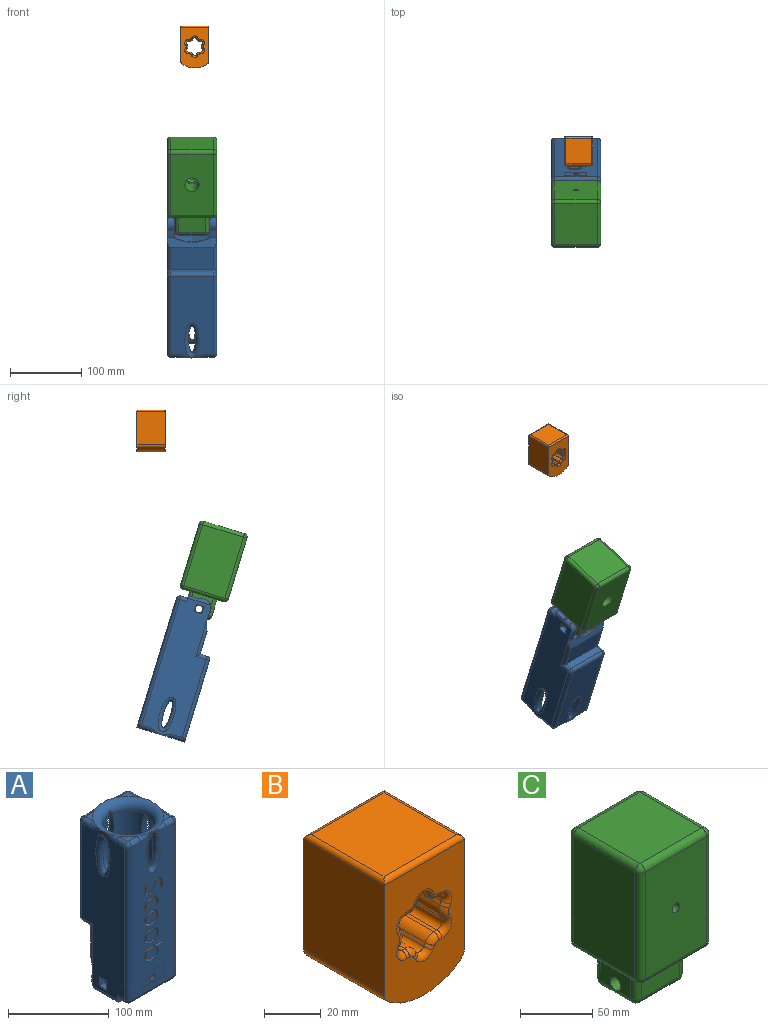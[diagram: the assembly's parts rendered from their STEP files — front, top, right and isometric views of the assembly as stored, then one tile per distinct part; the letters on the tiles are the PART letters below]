
ASSEMBLY  parts=3 mates=1
PART A: 199 faces, bbox 111.1x111.1x220.2 mm
  f0: plane 215x80mm, normal (-1,0,0), area 9348.8mm2, adj f3,f12,f14,f16,f42,f46,f49,f50
  f1: plane 60x32.41mm, normal (0,1,0), area 1944.7mm2, adj f10,f16,f28,f191
  f2: plane 10x8.52mm, normal (0,-1,0), area 37.4mm2, adj f4,f7,f30,f59,f197
  f3: plane 10x8.52mm, normal (0,-1,0), area 37.4mm2, adj f0,f12,f30,f56,f195
  f4: plane 215x80mm, normal (1,0,0), area 9383.2mm2, adj f2,f7,f8,f10,f24,f34,f36,f39
  f5: plane 60x45mm, normal (-1,0,0), area 792.6mm2, adj f7,f9,f11,f24,f29,f30,f31,f68
  f6: plane 60x45mm, normal (1,0,0), area 792.6mm2, adj f12,f15,f17,f23,f29,f30,f31,f68
  f7: cylinder r=5mm len=33.8mm, axis (0,-1,0), area 340.7mm2, adj f2,f4,f5,f194,f197,f198
  f8: cylinder r=5mm len=11.1mm, axis (0,0,-1), area 0mm2, adj f4,f194
  f9: cylinder r=5mm len=11.1mm, axis (0,0,-1), area 0mm2, adj f5,f194
  f10: cylinder r=5mm len=50.66mm, axis (0,0,-1), area 326.2mm2, adj f1,f4,f39,f191
  f11: cylinder r=5mm len=0.66mm, axis (0,0,-1), area 0.1mm2, adj f5,f13,f191
  f12: cylinder r=5mm len=33.8mm, axis (0,-1,0), area 340.7mm2, adj f0,f3,f6,f192,f195,f196
  f13: bspline ~64.63x12.82mm, area 80.3mm2, adj f11,f17,f31,f191
  f14: cylinder r=5mm len=11.1mm, axis (0,0,1), area 0mm2, adj f0,f192
  f15: cylinder r=5mm len=11.1mm, axis (0,0,1), area 0mm2, adj f6,f192
  f16: cylinder r=5mm len=50.66mm, axis (0,0,1), area 326.2mm2, adj f0,f1,f42,f191
  f17: cylinder r=5mm len=0.66mm, axis (0,0,1), area 0.1mm2, adj f6,f13,f191
  f18: plane 190x60mm, normal (0,-1,0), area 8811.1mm2, adj f52,f54,f57,f60,f64,f66,f67,f76
  f19: plane 11.97x11.97mm, normal (0,0,1), area 59.9mm2, adj f32,f63,f66
  f20: plane 11.97x11.97mm, normal (0,0,1), area 59.9mm2, adj f32,f53,f54
  f21: plane 11.97x11.97mm, normal (0,0,1), area 59.9mm2, adj f32,f47,f49
  f22: plane 120x60mm, normal (0,1,0), area 6147.2mm2, adj f35,f37,f40,f43,f45,f46,f47,f73
  f23: cylinder r=5.25mm len=10.5mm, axis (-1,0,0), area 99mm2, adj f6,f189
  f24: cylinder r=5.25mm len=10.5mm, axis (-1,0,0), area 329.9mm2, adj f4,f5
  f25: plane 11.97x11.97mm, normal (0,0,1), area 59.9mm2, adj f32,f36,f37
  f26: cylinder r=25mm len=105mm, axis (0,0,1), area 15263.1mm2, adj f32,f33,f69,f70,f71,f72
  f27: plane 40x40mm, normal (0,0,1), area 1256.6mm2, adj f33
  f28: plane 60x10mm, normal (0,0,-1), area 600mm2, adj f1,f39,f42,f43
  f29: plane 50x25.26mm, normal (0,1,0), area 979.4mm2, adj f5,f6,f31,f68,f184
  f30: plane 60x10mm, normal (0,0,-1), area 350mm2, adj f2,f3,f5,f6,f56,f59,f60,f68
  f31: extruded ~50x35mm, area 1791.2mm2, adj f5,f6,f13,f29
  f32: torus R=35mm, axis (0,0,-1), area 2792.6mm2, adj f19,f20,f21,f25,f26,f34,f35,f45
  f33: torus R=20mm, axis (0,0,1), area 1144mm2, adj f26,f27
  f34: bspline ~18.62x5.29mm, area 43.9mm2, adj f4,f32,f36
  f35: bspline ~18.62x5.29mm, area 45.1mm2, adj f22,f32,f37
  f36: cylinder r=5mm len=11.97mm, axis (0,-1,0), area 94mm2, adj f4,f25,f34,f38
  f37: cylinder r=5mm len=11.97mm, axis (1,0,0), area 94mm2, adj f22,f25,f35,f38
  f38: sphere r=5mm, area 39.3mm2, adj f36,f37,f40
  f39: cylinder r=5mm len=15mm, axis (0,-1,0), area 98.2mm2, adj f4,f10,f28,f41
  f40: cylinder r=5mm len=115mm, axis (0,0,-1), area 903.2mm2, adj f4,f22,f38,f41
  f41: sphere r=5mm, area 39.3mm2, adj f39,f40,f43
  f42: cylinder r=5mm len=15mm, axis (0,1,0), area 98.2mm2, adj f0,f16,f28,f44
  f43: cylinder r=5mm len=60mm, axis (-1,0,0), area 471.2mm2, adj f22,f28,f41,f44
  f44: sphere r=5mm, area 49.3mm2, adj f42,f43,f46
  f45: bspline ~18.03x5mm, area 45.1mm2, adj f22,f32,f47
  f46: cylinder r=5mm len=115mm, axis (0,0,1), area 903.2mm2, adj f0,f22,f44,f48
  f47: cylinder r=5mm len=11.97mm, axis (1,0,0), area 94mm2, adj f21,f22,f45,f48
  f48: sphere r=5mm, area 39.3mm2, adj f46,f47,f49
  f49: cylinder r=5mm len=11.97mm, axis (0,1,0), area 94mm2, adj f0,f21,f48,f50
  f50: bspline ~18.03x5mm, area 43.9mm2, adj f0,f32,f49
  f51: bspline ~18.03x5mm, area 45.1mm2, adj f0,f32,f53
  f52: bspline ~18.62x5.29mm, area 45.1mm2, adj f18,f32,f54
  f53: cylinder r=5mm len=11.97mm, axis (0,1,0), area 94mm2, adj f0,f20,f51,f55
  f54: cylinder r=5mm len=11.97mm, axis (-1,0,0), area 94mm2, adj f18,f20,f52,f55
  f55: sphere r=5mm, area 53.5mm2, adj f53,f54,f57
  f56: cylinder r=5mm len=10mm, axis (0,1,0), area 78.5mm2, adj f0,f3,f30,f58
  f57: cylinder r=5mm len=185mm, axis (0,0,-1), area 1453mm2, adj f0,f18,f55,f58
  f58: sphere r=5mm, area 53.5mm2, adj f56,f57,f60
  f59: cylinder r=5mm len=10mm, axis (0,-1,0), area 78.5mm2, adj f2,f4,f30,f62
  f60: cylinder r=5mm len=60mm, axis (-1,0,0), area 471.2mm2, adj f18,f30,f58,f62
  f61: bspline ~18.62x5.29mm, area 45.1mm2, adj f4,f32,f63
  f62: sphere r=5mm, area 25mm2, adj f59,f60,f64
  f63: cylinder r=5mm len=11.97mm, axis (0,-1,0), area 94mm2, adj f4,f19,f61,f65
  f64: cylinder r=5mm len=185mm, axis (0,0,1), area 1453mm2, adj f4,f18,f62,f65
  f65: sphere r=5mm, area 25mm2, adj f63,f64,f66
  f66: cylinder r=5mm len=11.97mm, axis (-1,0,0), area 94mm2, adj f18,f19,f65,f67
  f67: bspline ~18.03x5mm, area 45.1mm2, adj f18,f32,f66
  f68: cylinder r=5mm len=50mm, axis (-1,0,0), area 392.7mm2, adj f5,f6,f29,f30
  f69: extruded ~39.82x9.96mm, area 457.4mm2, adj f26,f32,f73
  f70: extruded ~39.82x9.96mm, area 457.4mm2, adj f26,f32,f76
  f71: extruded ~39.82x9.96mm, area 456.4mm2, adj f26,f75
  f72: extruded ~40x10mm, area 456.5mm2, adj f26,f74
  f73: bspline ~50x20.01mm, area 763.5mm2, adj f22,f69
  f74: bspline ~50x20.01mm, area 763.5mm2, adj f0,f72
  f75: bspline ~50x20.01mm, area 763.5mm2, adj f4,f71
  f76: bspline ~50x20.01mm, area 763.5mm2, adj f18,f70
  f77: plane 30x15mm, normal (0,-1,0), area 405.8mm2, adj f18,f183
  f78: extruded ~7.08x5.13mm, area 39.1mm2, adj f18,f79,f94,f95
  f79: extruded ~6.25x5.13mm, area 35.9mm2, adj f18,f78,f80,f95
  f80: extruded ~6.36x5.13mm, area 36.3mm2, adj f18,f79,f81,f95
  f81: extruded ~7.14x5.13mm, area 39.4mm2, adj f18,f80,f82,f95
  f82: extruded ~5.17x5.13mm, area 27.3mm2, adj f18,f81,f83,f95
  f83: extruded ~5.13x3.39mm, area 23.6mm2, adj f18,f82,f84,f95
  f84: extruded ~5.13x4.47mm, area 24mm2, adj f18,f83,f85,f95
  f85: extruded ~6.38x5.13mm, area 36.4mm2, adj f18,f84,f94,f95
  f86: extruded ~5.45x5.13mm, area 29.4mm2, adj f87,f93,f95,f180
  f87: extruded ~5.13x4.21mm, area 24.4mm2, adj f86,f88,f95,f180
  f88: extruded ~5.13x4.27mm, area 24.8mm2, adj f87,f89,f95,f180
  f89: extruded ~5.43x5.13mm, area 29.4mm2, adj f88,f90,f95,f180
  f90: extruded ~5.48x5.13mm, area 29.6mm2, adj f89,f91,f95,f180
  f91: extruded ~5.13x4.24mm, area 24.7mm2, adj f90,f92,f95,f180
  f92: extruded ~5.13x4.22mm, area 24.6mm2, adj f91,f93,f95,f180
  f93: extruded ~5.48x5.13mm, area 29.6mm2, adj f86,f92,f95,f180
  f94: extruded ~7.16x5.13mm, area 39.5mm2, adj f18,f78,f85,f95
  f95: plane 19.43x17.22mm, normal (0,-1,0), area 134.9mm2, adj f78,f79,f80,f81,f82,f83,f84,f85
  f96: extruded ~7.08x5.13mm, area 39.1mm2, adj f18,f97,f112,f113
  f97: extruded ~6.25x5.13mm, area 35.9mm2, adj f18,f96,f98,f113
  f98: extruded ~6.36x5.13mm, area 36.3mm2, adj f18,f97,f99,f113
  f99: extruded ~7.14x5.13mm, area 39.4mm2, adj f18,f98,f100,f113
  f100: extruded ~5.17x5.13mm, area 27.3mm2, adj f18,f99,f101,f113
  f101: extruded ~5.13x3.39mm, area 23.6mm2, adj f18,f100,f102,f113
  f102: extruded ~5.13x4.47mm, area 24mm2, adj f18,f101,f103,f113
  f103: extruded ~6.38x5.13mm, area 36.4mm2, adj f18,f102,f112,f113
  f104: extruded ~5.45x5.13mm, area 29.4mm2, adj f105,f111,f113,f181
  f105: extruded ~5.13x4.21mm, area 24.4mm2, adj f104,f106,f113,f181
  f106: extruded ~5.13x4.27mm, area 24.8mm2, adj f105,f107,f113,f181
  f107: extruded ~5.43x5.13mm, area 29.4mm2, adj f106,f108,f113,f181
  f108: extruded ~5.48x5.13mm, area 29.6mm2, adj f107,f109,f113,f181
  f109: extruded ~5.13x4.24mm, area 24.7mm2, adj f108,f110,f113,f181
  f110: extruded ~5.13x4.22mm, area 24.6mm2, adj f109,f111,f113,f181
  f111: extruded ~5.48x5.13mm, area 29.6mm2, adj f104,f110,f113,f181
  f112: extruded ~7.16x5.13mm, area 39.5mm2, adj f18,f96,f103,f113
  f113: plane 19.43x17.22mm, normal (0,-1,0), area 134.9mm2, adj f96,f97,f98,f99,f100,f101,f102,f103
  f114: extruded ~5.13x4.73mm, area 25.1mm2, adj f18,f115,f128,f129
  f115: plane 5.13x2.51mm, normal (0,0,1), area 12.9mm2, adj f18,f114,f116,f129
  f116: extruded ~5.13x4.81mm, area 25.4mm2, adj f18,f115,f117,f129
  f117: extruded ~5.13x4.13mm, area 24.1mm2, adj f18,f116,f118,f129
  f118: extruded ~5.3x5.13mm, area 28.6mm2, adj f18,f117,f119,f129
  f119: extruded ~7.28x5.71mm, area 54.3mm2, adj f18,f118,f120,f129
  f120: extruded ~5.13x1.96mm, area 10.2mm2, adj f18,f119,f121,f129
  f121: extruded ~5.13x2.05mm, area 11mm2, adj f18,f120,f122,f129
  f122: plane 5.13x2.41mm, normal (0.34,0,0.94), area 13.1mm2, adj f18,f121,f123,f129
  f123: extruded ~5.13x2.12mm, area 11.5mm2, adj f18,f122,f124,f129
  f124: extruded ~5.13x2.7mm, area 14mm2, adj f18,f123,f125,f129
  f125: extruded ~6.46x5.13mm, area 36.8mm2, adj f18,f124,f126,f129
  f126: extruded ~7.27x5.13mm, area 40mm2, adj f18,f125,f127,f129
  f127: extruded ~7.09x5.13mm, area 39mm2, adj f18,f126,f128,f129
  f128: extruded ~6.3x5.13mm, area 35.9mm2, adj f18,f114,f127,f129
  f129: plane 19.43x13.54mm, normal (0,-1,0), area 93.2mm2, adj f114,f115,f116,f117,f118,f119,f120,f121
  f130: extruded ~5.88x5.13mm, area 34.9mm2, adj f18,f131,f152,f153
  f131: plane 5.13x0.14mm, normal (-1,0,0), area 0.7mm2, adj f18,f130,f132,f153
  f132: extruded ~5.13x3.9mm, area 20mm2, adj f18,f131,f133,f153
  f133: plane 6.47x5.13mm, normal (0,0,1), area 33.2mm2, adj f18,f132,f134,f153
  f134: plane 5.13x2.84mm, normal (-1,0,0), area 14.6mm2, adj f18,f133,f135,f153
  f135: plane 26.61x5.13mm, normal (0,0,-1), area 136.6mm2, adj f18,f134,f136,f153
  f136: plane 5.13x2.04mm, normal (1,0,0), area 10.5mm2, adj f18,f135,f137,f153
  f137: plane 5.13x2.41mm, normal (0.24,0,0.97), area 12.8mm2, adj f18,f136,f138,f153
  f138: plane 5.13x0.21mm, normal (1,0,0), area 1.1mm2, adj f18,f137,f139,f153
  f139: extruded ~5.13x2.54mm, area 17mm2, adj f18,f138,f140,f153
  f140: extruded ~5.13x3.35mm, area 17.7mm2, adj f18,f139,f141,f153
  f141: extruded ~5.72x5.13mm, area 33.4mm2, adj f18,f140,f142,f153
  f142: extruded ~7.18x5.13mm, area 39.1mm2, adj f18,f141,f143,f153
  f143: extruded ~7.14x5.13mm, area 38.9mm2, adj f18,f142,f152,f153
  f144: extruded ~5.13x3.97mm, area 23.3mm2, adj f145,f151,f153,f182
  f145: extruded ~5.46x5.13mm, area 29.2mm2, adj f144,f146,f153,f182
  f146: extruded ~5.48x5.13mm, area 29.3mm2, adj f145,f147,f153,f182
  f147: extruded ~5.13x3.9mm, area 23.3mm2, adj f146,f148,f153,f182
  f148: extruded ~5.13x4.22mm, area 24.2mm2, adj f147,f149,f153,f182
  f149: extruded ~5.65x5.13mm, area 30.3mm2, adj f148,f150,f153,f182
  f150: extruded ~5.62x5.13mm, area 30.1mm2, adj f149,f151,f153,f182
  f151: extruded ~5.13x4.19mm, area 24mm2, adj f144,f150,f153,f182
  f152: extruded ~5.74x5.13mm, area 33.3mm2, adj f18,f130,f143,f153
  f153: plane 26.96x16.51mm, normal (0,-1,0), area 170.7mm2, adj f130,f131,f132,f133,f134,f135,f136,f137
  f154: extruded ~5.13x4.17mm, area 23.3mm2, adj f18,f155,f178,f179
  f155: extruded ~5.41x5.13mm, area 32.1mm2, adj f18,f154,f156,f179
  f156: extruded ~5.13x3.48mm, area 19.5mm2, adj f18,f155,f157,f179
  f157: extruded ~5.13x1.62mm, area 11.5mm2, adj f18,f156,f158,f179
  f158: extruded ~5.13x2.13mm, area 11.3mm2, adj f18,f157,f159,f179
  f159: extruded ~5.13x2.75mm, area 16.2mm2, adj f18,f158,f160,f179
  f160: extruded ~5.13x3.61mm, area 19.6mm2, adj f18,f159,f161,f179
  f161: extruded ~6.02x5.13mm, area 31.8mm2, adj f18,f160,f162,f179
  f162: plane 5.13x2.53mm, normal (0.34,0,0.94), area 13.8mm2, adj f18,f161,f163,f179
  f163: extruded ~6.86x5.13mm, area 36.2mm2, adj f18,f162,f164,f179
  f164: extruded ~5.75x5.13mm, area 31.4mm2, adj f18,f163,f165,f179
  f165: extruded ~5.13x4.6mm, area 27.1mm2, adj f18,f164,f166,f179
  f166: extruded ~5.13x4.46mm, area 24.7mm2, adj f18,f165,f167,f179
  f167: extruded ~5.13x4.98mm, area 30mm2, adj f18,f166,f168,f179
  f168: extruded ~5.13x3.72mm, area 20.8mm2, adj f18,f167,f169,f179
  f169: extruded ~5.13x1.75mm, area 12mm2, adj f18,f168,f170,f179
  f170: extruded ~5.13x2.13mm, area 11.4mm2, adj f18,f169,f171,f179
  f171: extruded ~5.13x3.07mm, area 18.2mm2, adj f18,f170,f172,f179
  f172: extruded ~5.13x4.38mm, area 23.6mm2, adj f18,f171,f173,f179
  f173: extruded ~5.13x3.59mm, area 18.6mm2, adj f18,f172,f174,f179
  f174: extruded ~5.13x3.35mm, area 18mm2, adj f18,f173,f175,f179
  f175: plane 5.13x2.8mm, normal (0,0,-1), area 14.4mm2, adj f18,f174,f176,f179
  f176: extruded ~6.84x5.13mm, area 35.9mm2, adj f18,f175,f177,f179
  f177: extruded ~6.5x5.13mm, area 35.3mm2, adj f18,f176,f178,f179
  f178: extruded ~5.15x5.13mm, area 30.3mm2, adj f18,f154,f177,f179
  f179: plane 25.7x15.73mm, normal (0,-1,0), area 144.7mm2, adj f154,f155,f156,f157,f158,f159,f160,f161
  f180: plane 14.64x11.34mm, normal (0,-1,0), area 137.7mm2, adj f86,f87,f88,f89,f90,f91,f92,f93
  f181: plane 14.64x11.34mm, normal (0,-1,0), area 137.7mm2, adj f104,f105,f106,f107,f108,f109,f110,f111
  f182: plane 14.64x10.72mm, normal (0,-1,0), area 132.2mm2, adj f144,f145,f146,f147,f148,f149,f150,f151
  f183: cylinder r=3.75mm len=11.25mm, axis (0,1,0), area 265.1mm2, adj f77,f184
  f184: cone r=3.75mm half-angle=45deg, axis (0,1,0), area 187.4mm2, adj f29,f183
  f185: plane 11x7mm, normal (0,0,-1), area 77mm2, adj f0,f186,f188,f189
  f186: plane 11x7mm, normal (0,-1,0), area 77mm2, adj f0,f185,f187,f189
  f187: plane 11x7mm, normal (0,0,1), area 77mm2, adj f0,f186,f188,f189
  f188: plane 11x7mm, normal (0,1,0), area 77mm2, adj f0,f185,f187,f189
  f189: plane 11x11mm, normal (-1,0,0), area 34.4mm2, adj f23,f185,f186,f187,f188
  f190: plane 11.12x10mm, normal (0,1,0), area 111.2mm2, adj f0,f6,f191,f192
  f191: plane 75.57x18.81mm, normal (0,0.94,-0.35), area 742.8mm2, adj f1,f10,f11,f13,f16,f17,f190,f193
  f192: cylinder r=13.47mm len=18.23mm, axis (1,0,0), area 199.7mm2, adj f0,f6,f12,f14,f15,f190
  f193: plane 11.12x10mm, normal (0,1,0), area 111.2mm2, adj f4,f5,f191,f194
  f194: cylinder r=13.47mm len=18.23mm, axis (1,0,0), area 199.7mm2, adj f4,f5,f7,f8,f9,f193
  f195: plane 15.23x7.1mm, normal (0,0,-1), area 108.2mm2, adj f3,f12,f196
  f196: cylinder r=13.47mm len=7.1mm, axis (1,0,0), area 15.3mm2, adj f12,f195
  f197: plane 15.23x7.1mm, normal (0,0,-1), area 108.2mm2, adj f2,f7,f198
  f198: cylinder r=13.47mm len=7.1mm, axis (1,0,0), area 15.3mm2, adj f7,f197
PART B: 84 faces, bbox 40x40x59.1 mm
  f0: plane 57.1x40mm, normal (0,-1,0), area 1580.3mm2, adj f2,f3,f5,f24,f25,f26,f27,f29
  f1: plane 57.1x40mm, normal (0,1,0), area 1580.3mm2, adj f2,f3,f5,f28,f32,f33,f37,f38
  f2: plane 47.1x40mm, normal (-1,0,0), area 1884mm2, adj f0,f1,f78,f81
  f3: plane 47.1x40mm, normal (1,0,0), area 1884mm2, adj f0,f1,f79,f82
  f4: plane 36x36mm, normal (0,0,1), area 1296mm2, adj f80,f81,f82,f83
  f5: cylinder r=30mm len=40mm, axis (0,-1,0), area 1544.4mm2, adj f0,f1,f78,f79
  f6: plane 35x1.35mm, normal (0.87,0,0.5), area 54.6mm2, adj f23,f52,f53,f62
  f7: plane 35x1.35mm, normal (-0.87,0,0.5), area 54.6mm2, adj f18,f43,f51,f52
  f8: plane 35x1.56mm, normal (0,0,1), area 54.6mm2, adj f18,f34,f35,f42
  f9: plane 35x1.35mm, normal (-0.87,0,-0.5), area 54.6mm2, adj f19,f26,f33,f34
  f10: plane 35x1.35mm, normal (-0.87,0,0.5), area 54.6mm2, adj f19,f25,f31,f32
  f11: plane 35x1.56mm, normal (0,0,-1), area 54.6mm2, adj f20,f30,f31,f41
  f12: plane 35x1.35mm, normal (-0.87,0,-0.5), area 54.6mm2, adj f20,f40,f49,f50
  f13: plane 35x1.35mm, normal (0.87,0,-0.5), area 54.6mm2, adj f21,f48,f49,f61
  f14: plane 35x1.56mm, normal (0,0,-1), area 54.6mm2, adj f21,f60,f69,f70
  f15: plane 35x1.35mm, normal (0.87,0,0.5), area 54.6mm2, adj f22,f59,f69,f75
  f16: plane 35x1.35mm, normal (0.87,0,-0.5), area 54.6mm2, adj f22,f64,f72,f76
  f17: plane 35x1.56mm, normal (0,0,1), area 54.6mm2, adj f23,f63,f71,f72
  f18: cylinder r=5mm len=35mm, axis (0,-1,0), area 183.3mm2, adj f7,f8,f39,f46
  f19: cylinder r=5mm len=35mm, axis (0,-1,0), area 183.3mm2, adj f9,f10,f24,f28
  f20: cylinder r=5mm len=35mm, axis (0,-1,0), area 183.3mm2, adj f11,f12,f36,f45
  f21: cylinder r=5mm len=35mm, axis (0,-1,0), area 183.3mm2, adj f13,f14,f54,f66
  f22: cylinder r=5mm len=35mm, axis (0,-1,0), area 183.3mm2, adj f15,f16,f58,f77
  f23: cylinder r=5mm len=35mm, axis (0,-1,0), area 183.3mm2, adj f6,f17,f57,f67
  f24: torus R=2.5mm, axis (0,1,0), area 16.8mm2, adj f0,f19,f25,f26
  f25: cylinder r=2.5mm len=2.94mm, axis (0.5,0,0.87), area 6.1mm2, adj f0,f10,f24,f27
  f26: cylinder r=2.5mm len=2.94mm, axis (-0.5,0,0.87), area 6.1mm2, adj f0,f9,f24,f29
  f27: torus R=5mm, axis (0,1,0), area 28mm2, adj f0,f25,f30,f31
  f28: torus R=2.5mm, axis (0,1,0), area 16.8mm2, adj f1,f19,f32,f33
  f29: torus R=5mm, axis (0,1,0), area 28mm2, adj f0,f26,f34,f35
  f30: cylinder r=2.5mm len=2.5mm, axis (-1,0,0), area 6.1mm2, adj f0,f11,f27,f36
  f31: cylinder r=2.5mm len=35mm, axis (0,-1,0), area 183.3mm2, adj f10,f11,f27,f37
  f32: cylinder r=2.5mm len=2.94mm, axis (0.5,0,0.87), area 6.1mm2, adj f1,f10,f28,f37
  f33: cylinder r=2.5mm len=2.94mm, axis (-0.5,0,0.87), area 6.1mm2, adj f1,f9,f28,f38
  f34: cylinder r=2.5mm len=35mm, axis (0,1,0), area 183.3mm2, adj f8,f9,f29,f38
  f35: cylinder r=2.5mm len=2.5mm, axis (1,0,0), area 6.1mm2, adj f0,f8,f29,f39
  f36: torus R=2.5mm, axis (0,1,0), area 16.8mm2, adj f0,f20,f30,f40
  f37: torus R=5mm, axis (0,1,0), area 28mm2, adj f1,f31,f32,f41
  f38: torus R=5mm, axis (0,1,0), area 28mm2, adj f1,f33,f34,f42
  f39: torus R=2.5mm, axis (0,1,0), area 16.8mm2, adj f0,f18,f35,f43
  f40: cylinder r=2.5mm len=2.94mm, axis (-0.5,0,0.87), area 6.1mm2, adj f0,f12,f36,f44
  f41: cylinder r=2.5mm len=2.5mm, axis (-1,0,0), area 6.1mm2, adj f1,f11,f37,f45
  f42: cylinder r=2.5mm len=2.5mm, axis (1,0,0), area 6.1mm2, adj f1,f8,f38,f46
  f43: cylinder r=2.5mm len=2.94mm, axis (0.5,0,0.87), area 6.1mm2, adj f0,f7,f39,f47
  f44: torus R=5mm, axis (0,1,0), area 28mm2, adj f0,f40,f48,f49
  f45: torus R=2.5mm, axis (0,1,0), area 16.8mm2, adj f1,f20,f41,f50
  f46: torus R=2.5mm, axis (0,1,0), area 16.8mm2, adj f1,f18,f42,f51
  f47: torus R=5mm, axis (0,1,0), area 28mm2, adj f0,f43,f52,f53
  f48: cylinder r=2.5mm len=2.94mm, axis (-0.5,0,-0.87), area 6.1mm2, adj f0,f13,f44,f54
  f49: cylinder r=2.5mm len=35mm, axis (0,-1,0), area 183.3mm2, adj f12,f13,f44,f55
  f50: cylinder r=2.5mm len=2.94mm, axis (-0.5,0,0.87), area 6.1mm2, adj f1,f12,f45,f55
  f51: cylinder r=2.5mm len=2.94mm, axis (0.5,0,0.87), area 6.1mm2, adj f1,f7,f46,f56
  f52: cylinder r=2.5mm len=35mm, axis (0,-1,0), area 183.3mm2, adj f6,f7,f47,f56
  f53: cylinder r=2.5mm len=2.94mm, axis (0.5,0,-0.87), area 6.1mm2, adj f0,f6,f47,f57
  f54: torus R=2.5mm, axis (0,1,0), area 16.8mm2, adj f0,f21,f48,f60
  f55: torus R=5mm, axis (0,1,0), area 28mm2, adj f1,f49,f50,f61
  f56: torus R=5mm, axis (0,1,0), area 28mm2, adj f1,f51,f52,f62
  f57: torus R=2.5mm, axis (0,1,0), area 16.8mm2, adj f0,f23,f53,f63
  f58: torus R=2.5mm, axis (0,1,0), area 16.8mm2, adj f0,f22,f59,f64
  f59: cylinder r=2.5mm len=2.94mm, axis (0.5,0,-0.87), area 6.1mm2, adj f0,f15,f58,f65
  f60: cylinder r=2.5mm len=2.5mm, axis (-1,0,0), area 6.1mm2, adj f0,f14,f54,f65
  f61: cylinder r=2.5mm len=2.94mm, axis (-0.5,0,-0.87), area 6.1mm2, adj f1,f13,f55,f66
  f62: cylinder r=2.5mm len=2.94mm, axis (0.5,0,-0.87), area 6.1mm2, adj f1,f6,f56,f67
  f63: cylinder r=2.5mm len=2.5mm, axis (1,0,0), area 6.1mm2, adj f0,f17,f57,f68
  f64: cylinder r=2.5mm len=2.94mm, axis (-0.5,0,-0.87), area 6.1mm2, adj f0,f16,f58,f68
  f65: torus R=5mm, axis (0,1,0), area 28mm2, adj f0,f59,f60,f69
  f66: torus R=2.5mm, axis (0,1,0), area 16.8mm2, adj f1,f21,f61,f70
  f67: torus R=2.5mm, axis (0,1,0), area 16.8mm2, adj f1,f23,f62,f71
  f68: torus R=5mm, axis (0,1,0), area 28mm2, adj f0,f63,f64,f72
  f69: cylinder r=2.5mm len=35mm, axis (0,1,0), area 183.3mm2, adj f14,f15,f65,f73
  f70: cylinder r=2.5mm len=2.5mm, axis (-1,0,0), area 6.1mm2, adj f1,f14,f66,f73
  f71: cylinder r=2.5mm len=2.5mm, axis (1,0,0), area 6.1mm2, adj f1,f17,f67,f74
  f72: cylinder r=2.5mm len=35mm, axis (0,-1,0), area 183.3mm2, adj f16,f17,f68,f74
  f73: torus R=5mm, axis (0,1,0), area 28mm2, adj f1,f69,f70,f75
  f74: torus R=5mm, axis (0,1,0), area 28mm2, adj f1,f71,f72,f76
  f75: cylinder r=2.5mm len=2.94mm, axis (0.5,0,-0.87), area 6.1mm2, adj f1,f15,f73,f77
  f76: cylinder r=2.5mm len=2.94mm, axis (-0.5,0,-0.87), area 6.1mm2, adj f1,f16,f74,f77
  f77: torus R=2.5mm, axis (0,1,0), area 16.8mm2, adj f1,f22,f75,f76
  f78: cylinder r=5mm len=40mm, axis (0,-1,0), area 185.5mm2, adj f0,f1,f2,f5
  f79: cylinder r=5mm len=40mm, axis (0,-1,0), area 185.5mm2, adj f0,f1,f3,f5
  f80: cylinder r=2mm len=40mm, axis (1,0,0), area 121.1mm2, adj f1,f4,f81,f82
  f81: cylinder r=2mm len=40mm, axis (0,1,0), area 121.1mm2, adj f2,f4,f80,f83
  f82: cylinder r=2mm len=40mm, axis (0,-1,0), area 121.1mm2, adj f3,f4,f80,f83
  f83: cylinder r=2mm len=40mm, axis (-1,0,0), area 121.1mm2, adj f0,f4,f81,f82
PART C: 48 faces, bbox 70x70x130 mm
  f0: plane 90x60mm, normal (0,-1,0), area 5355.8mm2, adj f32,f37,f40,f43,f46
  f1: plane 90x60mm, normal (-1,0,0), area 5400mm2, adj f29,f38,f39,f43
  f2: plane 90x60mm, normal (0,1,0), area 5085.8mm2, adj f24,f28,f29,f30,f44
  f3: plane 90x60mm, normal (1,0,0), area 5400mm2, adj f24,f27,f31,f32
  f4: plane 60x60mm, normal (0,0,-1), area 1701.5mm2, adj f6,f7,f8,f9,f12,f14,f17,f23
  f5: plane 60x60mm, normal (0,0,1), area 3600mm2, adj f30,f31,f39,f40
  f6: plane 30x25mm, normal (-1,0,0), area 663.9mm2, adj f4,f11,f14,f20,f23
  f7: plane 38x25mm, normal (0,1,0), area 950mm2, adj f4,f17,f21,f23
  f8: plane 30x25mm, normal (1,0,0), area 663.9mm2, adj f4,f11,f12,f16,f17
  f9: plane 38x25mm, normal (0,-1,0), area 950mm2, adj f4,f12,f14,f15
  f10: plane 38x30mm, normal (0,0,-1), area 1140mm2, adj f15,f16,f20,f21
  f11: cylinder r=5.25mm len=48mm, axis (1,0,0), area 1583.4mm2, adj f6,f8,f16,f20
  f12: cylinder r=5mm len=25mm, axis (0,0,1), area 196.3mm2, adj f4,f8,f9,f13
  f13: sphere r=5mm, area 39.3mm2, adj f12,f15,f16
  f14: cylinder r=5mm len=25mm, axis (0,0,-1), area 196.3mm2, adj f4,f6,f9,f18
  f15: cylinder r=5mm len=38mm, axis (1,0,0), area 298.5mm2, adj f9,f10,f13,f18
  f16: cylinder r=5mm len=30mm, axis (0,1,0), area 235.1mm2, adj f8,f10,f11,f13,f19
  f17: cylinder r=5mm len=25mm, axis (0,0,-1), area 196.3mm2, adj f4,f7,f8,f19
  f18: sphere r=5mm, area 39.3mm2, adj f14,f15,f20
  f19: sphere r=5mm, area 39.3mm2, adj f16,f17,f21
  f20: cylinder r=5mm len=30mm, axis (0,-1,0), area 235.1mm2, adj f6,f10,f11,f18,f22
  f21: cylinder r=5mm len=38mm, axis (-1,0,0), area 298.5mm2, adj f7,f10,f19,f22
  f22: sphere r=5mm, area 39.3mm2, adj f20,f21,f23
  f23: cylinder r=5mm len=25mm, axis (0,0,1), area 196.3mm2, adj f4,f6,f7,f22
  f24: cylinder r=5mm len=90mm, axis (0,0,-1), area 706.9mm2, adj f2,f3,f25,f26
  f25: sphere r=5mm, area 39.3mm2, adj f24,f27,f28
  f26: sphere r=5mm, area 39.3mm2, adj f24,f30,f31
  f27: cylinder r=5mm len=60mm, axis (0,1,0), area 471.2mm2, adj f3,f4,f25,f33
  f28: cylinder r=5mm len=60mm, axis (-1,0,0), area 471.2mm2, adj f2,f4,f25,f34
  f29: cylinder r=5mm len=90mm, axis (0,0,1), area 706.9mm2, adj f1,f2,f34,f35
  f30: cylinder r=5mm len=60mm, axis (1,0,0), area 471.2mm2, adj f2,f5,f26,f35
  f31: cylinder r=5mm len=60mm, axis (0,-1,0), area 471.2mm2, adj f3,f5,f26,f36
  f32: cylinder r=5mm len=90mm, axis (0,0,1), area 706.9mm2, adj f0,f3,f33,f36
  f33: sphere r=5mm, area 39.3mm2, adj f27,f32,f37
  f34: sphere r=5mm, area 39.3mm2, adj f28,f29,f38
  f35: sphere r=5mm, area 39.3mm2, adj f29,f30,f39
  f36: sphere r=5mm, area 39.3mm2, adj f31,f32,f40
  f37: cylinder r=5mm len=60mm, axis (1,0,0), area 471.2mm2, adj f0,f4,f33,f41
  f38: cylinder r=5mm len=60mm, axis (0,-1,0), area 471.2mm2, adj f1,f4,f34,f41
  f39: cylinder r=5mm len=60mm, axis (0,1,0), area 471.2mm2, adj f1,f5,f35,f42
  f40: cylinder r=5mm len=60mm, axis (-1,0,0), area 471.2mm2, adj f0,f5,f36,f42
  f41: sphere r=5mm, area 39.3mm2, adj f37,f38,f43
  f42: sphere r=5mm, area 39.3mm2, adj f39,f40,f43
  f43: cylinder r=5mm len=90mm, axis (0,0,-1), area 706.9mm2, adj f0,f1,f41,f42
  f44: cylinder r=10mm len=35mm, axis (0,1,0), area 2199.1mm2, adj f2,f45
  f45: plane 20x20mm, normal (0,1,0), area 137.4mm2, adj f44,f47
  f46: cylinder r=3.75mm len=31.25mm, axis (0,1,0), area 736.3mm2, adj f0,f47
  f47: cone r=3.75mm half-angle=45deg, axis (0,1,0), area 187.4mm2, adj f45,f46
PLACE A rot(axis=(-1,0,0),163deg) t=(7.72,-74.74,-464.19)mm
PLACE B t=(7.45,-21.13,-51.05)mm
PLACE C rot(axis=(0,-0.15,0.99),180deg) t=(106.94,-161.88,-171.9)mm
MATE revolute A.f23 <-> C.f11  axis (-1,0,0) through (29.72,-76.39,-271.25)mm
